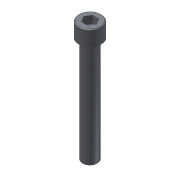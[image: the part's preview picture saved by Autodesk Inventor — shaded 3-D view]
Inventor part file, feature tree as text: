
AUTODESK INVENTOR PART (.ipt)
format: ipt  version: 2012 (Build 160160000, 160)  size: 102,912 bytes
history: native  units: in
note: dims shown in document units (in); Inventor stores cm internally (conversion verified against a paired STEP export)
features: extrude x3, sketch x3, fillet x1
ambient origin geometry x8: Origin, YZ Plane, XZ Plane, XY Plane, X Axis, Y Axis, Z Axis, Center Point
bodies: Solid1 (feature_tree)
feature tree (7):
  extrude  "Extrusion1"  Depth=1.75in TaperAngle=0.0deg
  extrude  "Extrusion2"  Depth=0.25in TaperAngle=0.0deg
  extrude  "Extrusion3"  Depth=0.125in TaperAngle=0.0deg
  fillet  "Fillet1"  Radius=0.0156in
  sketch  "Sketch1"  dims[d0=0.25in d1=1.75in d2=0.0in]
  sketch  "Sketch2"  dims[d3=0.375in d4=0.25in d5=0.0in]
  sketch  "Sketch3"  dims[d6=0.1875in d7=0.125in d8=0.0in d9=0.0156in]
